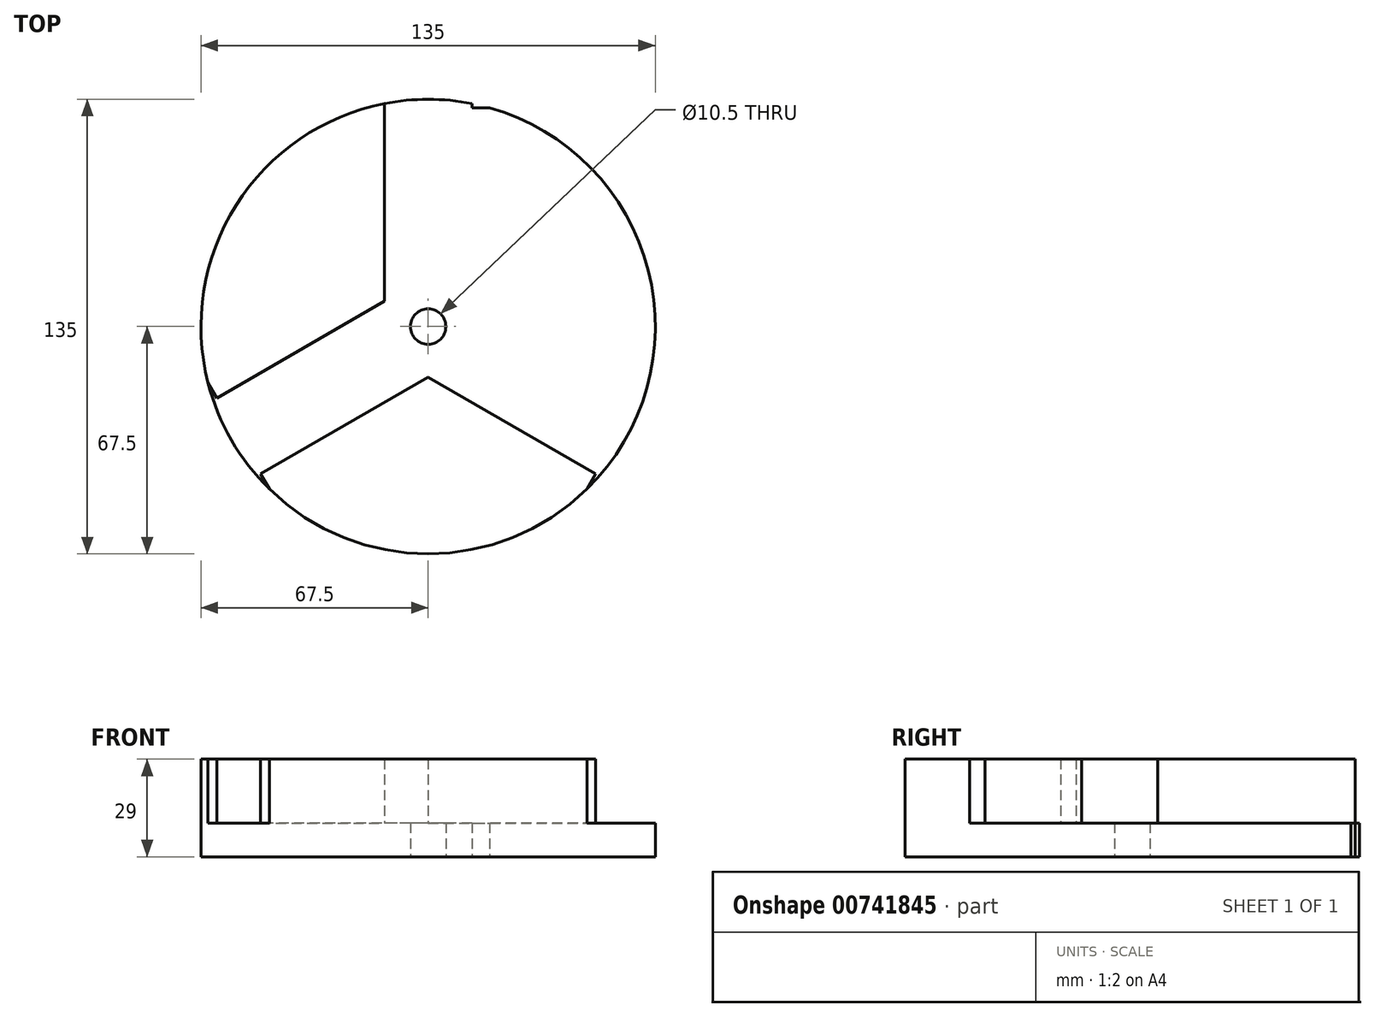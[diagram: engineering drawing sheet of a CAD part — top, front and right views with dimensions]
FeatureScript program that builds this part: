
annotation { "Feature Type Name" : "Feature", "Feature Type Description" : "" }
export const myFeature = defineFeature(function(context is Context, id is Id, definition is map)
    precondition{}
    {
        {
            var Q0;
            Q0=qCreatedBy(makeId("Top.planeOp"),FACE);
            var sketch = newSketch(context, id + "F0", { "sketchPlane" : qUnion([Q0])});
            skCircle(sketch, "E0", {"center": v(0, 0) * mm, "radius": 67.5 * mm});
            skCircle(sketch, "E1", {"center": v(0, 0) * mm, "radius": 5.25 * mm});
            skCircle(sketch, "E2", {"center": v(0, 0) * mm, "radius": 13 * mm});
            skLineSegment(sketch, "E3.top", {"start": v(-13, 70) * mm, "end": v(13, 70) * mm});
            skLineSegment(sketch, "E3.left", {"start": v(-13, 0) * mm, "end": v(-13, 70) * mm});
            skLineSegment(sketch, "E3.right", {"start": v(13, 0) * mm, "end": v(13, 70) * mm});
            skLineSegment(sketch, "E4", {"start": v(-6.5, 11.26) * mm, "end": v(-67.12, -23.74) * mm});
            skLineSegment(sketch, "E5", {"start": v(-67.12, -23.74) * mm, "end": v(-54.12, -46.26) * mm});
            skLineSegment(sketch, "E6", {"start": v(-54.12, -46.26) * mm, "end": v(6.5, -11.26) * mm});
            skLineSegment(sketch, "E7", {"start": v(6.5, 11.26) * mm, "end": v(67.12, -23.74) * mm});
            skLineSegment(sketch, "E8", {"start": v(67.12, -23.74) * mm, "end": v(54.12, -46.26) * mm});
            skLineSegment(sketch, "E9", {"start": v(54.12, -46.26) * mm, "end": v(-6.5, -11.26) * mm});
            skLineSegment(sketch, "E10", {"start": v(66.88, -14.17) * mm, "end": v(46.54, -49.38) * mm});
            skLineSegment(sketch, "E11", {"start": v(-65.4, -16.74) * mm, "end": v(-45.17, -51.75) * mm});
            skLineSegment(sketch, "E12", {"start": v(-20.7, 65) * mm, "end": v(22.29, 65) * mm});
            skCircle(sketch, "E13", {"center": v(0, 0) * mm, "radius": 6.25 * mm});
            skLineSegment(sketch, "E14", {"start": v(-13, 7.5) * mm, "end": v(-62.8, -21.24) * mm});
            skSolve(sketch);
        }
        {
            var Q0;
            {var subQ0=sQuery(id+"F0.wireOp",EDGE,"E12");var subQ1=sQuery(id+"F0.wireOp",EDGE,"E0");var subQ2=makeQuery(id+"F0.imprint","INTERSECT",VERTEX,{"disambiguationData":[OD(0.0)],"derivedFrom":[subQ1,subQ0]});Q0=makeQuery(id+"F0.imprint","IMPRINT",FACE,{"disambiguationData":[TD([[makeQuery(id+"F0.imprint","IMPRINT",EDGE,{"disambiguationData":[TD([[subQ2,-1.0]])],"derivedFrom":subQ1}),1.0]])]});}
            var Q1;
            {var subQ0=sQuery(id+"F0.wireOp",EDGE,"E12");var subQ1=sQuery(id+"F0.wireOp",EDGE,"E0");var subQ2=makeQuery(id+"F0.imprint","INTERSECT",VERTEX,{"disambiguationData":[OD(1.0)],"derivedFrom":[subQ1,subQ0]});Q1=makeQuery(id+"F0.imprint","IMPRINT",FACE,{"disambiguationData":[TD([[makeQuery(id+"F0.imprint","IMPRINT",EDGE,{"disambiguationData":[TD([[subQ2,1.0]])],"derivedFrom":subQ1}),1.0]])]});}
            var Q2;
            {var subQ0=sQuery(id+"F0.wireOp",EDGE,"E11");var subQ1=sQuery(id+"F0.wireOp",EDGE,"E0");var subQ2=makeQuery(id+"F0.imprint","INTERSECT",VERTEX,{"disambiguationData":[OD(0.0)],"derivedFrom":[subQ1,subQ0]});Q2=makeQuery(id+"F0.imprint","IMPRINT",FACE,{"disambiguationData":[TD([[makeQuery(id+"F0.imprint","IMPRINT",EDGE,{"disambiguationData":[TD([[subQ2,-1.0]])],"derivedFrom":subQ1}),1.0]])]});}
            var Q3;
            {var subQ0=sQuery(id+"F0.wireOp",EDGE,"E11");var subQ1=sQuery(id+"F0.wireOp",EDGE,"E0");var subQ2=makeQuery(id+"F0.imprint","INTERSECT",VERTEX,{"disambiguationData":[OD(1.0)],"derivedFrom":[subQ1,subQ0]});Q3=makeQuery(id+"F0.imprint","IMPRINT",FACE,{"disambiguationData":[TD([[makeQuery(id+"F0.imprint","IMPRINT",EDGE,{"disambiguationData":[TD([[subQ2,1.0]])],"derivedFrom":subQ1}),1.0]])]});}
            var Q4;
            {var subQ0=sQuery(id+"F0.wireOp",EDGE,"E10");var subQ1=sQuery(id+"F0.wireOp",EDGE,"E0");var subQ2=makeQuery(id+"F0.imprint","INTERSECT",VERTEX,{"disambiguationData":[OD(0.0)],"derivedFrom":[subQ1,subQ0]});Q4=makeQuery(id+"F0.imprint","IMPRINT",FACE,{"disambiguationData":[TD([[makeQuery(id+"F0.imprint","IMPRINT",EDGE,{"disambiguationData":[TD([[subQ2,-1.0]])],"derivedFrom":subQ1}),1.0]])]});}
            var Q5;
            {var subQ0=sQuery(id+"F0.wireOp",EDGE,"E10");var subQ1=sQuery(id+"F0.wireOp",EDGE,"E0");var subQ2=makeQuery(id+"F0.imprint","INTERSECT",VERTEX,{"disambiguationData":[OD(1.0)],"derivedFrom":[subQ1,subQ0]});Q5=makeQuery(id+"F0.imprint","IMPRINT",FACE,{"disambiguationData":[TD([[makeQuery(id+"F0.imprint","IMPRINT",EDGE,{"disambiguationData":[TD([[subQ2,1.0]])],"derivedFrom":subQ1}),1.0]])]});}
            var Q6;
            {var subQ5=sQuery(id+"F0.wireOp",EDGE,"E11");var subQ6=sQuery(id+"F0.wireOp",EDGE,"E0");var subQ7=makeQuery(id+"F0.imprint","INTERSECT",VERTEX,{"disambiguationData":[OD(0.0)],"derivedFrom":[subQ6,subQ5]});Q6=makeQuery(id+"F0.imprint","IMPRINT",FACE,{"disambiguationData":[TD([[makeQuery(id+"F0.imprint","IMPRINT",EDGE,{"disambiguationData":[TD([[subQ7,1.0]])],"derivedFrom":subQ6}),1.0]])]});}
            var Q7;
            {var subQ0=sQuery(id+"F0.wireOp",EDGE,"E4");var subQ1=sQuery(id+"F0.wireOp",EDGE,"E0");var subQ2=makeQuery(id+"F0.imprint","INTERSECT",VERTEX,{"derivedFrom":[subQ1,subQ0]});Q7=makeQuery(id+"F0.imprint","IMPRINT",FACE,{"disambiguationData":[TD([[makeQuery(id+"F0.imprint","IMPRINT",EDGE,{"disambiguationData":[TD([[subQ2,-1.0]])],"derivedFrom":subQ1}),1.0]])]});}
            var Q8;
            {var subQ5=sQuery(id+"F0.wireOp",EDGE,"E11");var subQ7=sQuery(id+"F0.wireOp",EDGE,"E0");var subQ9=makeQuery(id+"F0.imprint","INTERSECT",VERTEX,{"disambiguationData":[OD(1.0)],"derivedFrom":[subQ7,subQ5]});Q8=makeQuery(id+"F0.imprint","IMPRINT",FACE,{"disambiguationData":[TD([[makeQuery(id+"F0.imprint","IMPRINT",EDGE,{"disambiguationData":[TD([[subQ9,-1.0]])],"derivedFrom":subQ7}),1.0]])]});}
            var Q9;
            {var subQ0=sQuery(id+"F0.wireOp",EDGE,"E9");var subQ1=sQuery(id+"F0.wireOp",EDGE,"E0");var subQ2=makeQuery(id+"F0.imprint","INTERSECT",VERTEX,{"derivedFrom":[subQ1,subQ0]});Q9=makeQuery(id+"F0.imprint","IMPRINT",FACE,{"disambiguationData":[TD([[makeQuery(id+"F0.imprint","IMPRINT",EDGE,{"disambiguationData":[TD([[subQ2,-1.0]])],"derivedFrom":subQ1}),1.0]])]});}
            var Q10;
            {var subQ1=sQuery(id+"F0.wireOp",EDGE,"E0");var subQ7=sQuery(id+"F0.wireOp",EDGE,"E12");var subQ9=makeQuery(id+"F0.imprint","INTERSECT",VERTEX,{"disambiguationData":[OD(0.0)],"derivedFrom":[subQ1,subQ7]});Q10=makeQuery(id+"F0.imprint","IMPRINT",FACE,{"disambiguationData":[TD([[makeQuery(id+"F0.imprint","IMPRINT",EDGE,{"disambiguationData":[TD([[subQ9,1.0]])],"derivedFrom":subQ1}),1.0]])]});}
            var Q11;
            {var subQ0=sQuery(id+"F0.wireOp",EDGE,"E4");var subQ1=sQuery(id+"F0.wireOp",EDGE,"E2");var subQ2=makeQuery(id+"F0.imprint","INTERSECT",VERTEX,{"derivedFrom":[subQ1,subQ0]});Q11=makeQuery(id+"F0.imprint","IMPRINT",FACE,{"disambiguationData":[TD([[makeQuery(id+"F0.imprint","IMPRINT",EDGE,{"disambiguationData":[TD([[subQ2,1.0]])],"derivedFrom":subQ1}),-1.0]])]});}
            var Q12;
            {var subQ0=sQuery(id+"F0.wireOp",EDGE,"E3.right");var subQ1=sQuery(id+"F0.wireOp",EDGE,"E0");var subQ2=makeQuery(id+"F0.imprint","INTERSECT",VERTEX,{"derivedFrom":[subQ1,subQ0]});Q12=makeQuery(id+"F0.imprint","IMPRINT",FACE,{"disambiguationData":[TD([[makeQuery(id+"F0.imprint","IMPRINT",EDGE,{"disambiguationData":[TD([[subQ2,-1.0]])],"derivedFrom":subQ1}),1.0]])]});}
            var Q13;
            {var subQ0=sQuery(id+"F0.wireOp",EDGE,"E3.bottom");var subQ6=sQuery(id+"F0.wireOp",EDGE,"E1");var subQ7=makeQuery(id+"F0.imprint","INTERSECT",VERTEX,{"disambiguationData":[OD(0.0)],"derivedFrom":[subQ6,subQ0]});Q13=makeQuery(id+"F0.imprint","IMPRINT",FACE,{"disambiguationData":[TD([[makeQuery(id+"F0.imprint","IMPRINT",EDGE,{"disambiguationData":[TD([[subQ7,-1.0]])],"derivedFrom":subQ6}),-1.0]])]});}
            var Q14;
            {var subQ0=sQuery(id+"F0.wireOp",EDGE,"E4");var subQ1=sQuery(id+"F0.wireOp",EDGE,"E3.left");var subQ2=makeQuery(id+"F0.imprint","INTERSECT",VERTEX,{"derivedFrom":[subQ1,subQ0]});Q14=makeQuery(id+"F0.imprint","IMPRINT",FACE,{"disambiguationData":[TD([[makeQuery(id+"F0.imprint","IMPRINT",EDGE,{"disambiguationData":[TD([[subQ2,-1.0]])],"derivedFrom":subQ0}),1.0]])]});}
            var Q15;
            {var subQ0=sQuery(id+"F0.wireOp",EDGE,"E6");var subQ1=sQuery(id+"F0.wireOp",EDGE,"E2");var subQ2=makeQuery(id+"F0.imprint","INTERSECT",VERTEX,{"derivedFrom":[subQ1,subQ0]});Q15=makeQuery(id+"F0.imprint","IMPRINT",FACE,{"disambiguationData":[TD([[makeQuery(id+"F0.imprint","IMPRINT",EDGE,{"disambiguationData":[TD([[subQ2,1.0]])],"derivedFrom":subQ1}),-1.0]])]});}
            var Q16;
            {var subQ1=sQuery(id+"F0.wireOp",EDGE,"E2");var subQ3=sQuery(id+"F0.wireOp",EDGE,"E4");var subQ4=makeQuery(id+"F0.imprint","INTERSECT",VERTEX,{"derivedFrom":[subQ1,subQ3]});Q16=makeQuery(id+"F0.imprint","IMPRINT",FACE,{"disambiguationData":[TD([[makeQuery(id+"F0.imprint","IMPRINT",EDGE,{"disambiguationData":[TD([[subQ4,-1.0]])],"derivedFrom":subQ3}),1.0]])]});}
            var Q17;
            {var subQ1=sQuery(id+"F0.wireOp",EDGE,"E2");var subQ3=sQuery(id+"F0.wireOp",EDGE,"E7");var subQ4=makeQuery(id+"F0.imprint","INTERSECT",VERTEX,{"derivedFrom":[subQ1,subQ3]});Q17=makeQuery(id+"F0.imprint","IMPRINT",FACE,{"disambiguationData":[TD([[makeQuery(id+"F0.imprint","IMPRINT",EDGE,{"disambiguationData":[TD([[subQ4,-1.0]])],"derivedFrom":subQ3}),-1.0]])]});}
            var Q18;
            {var subQ0=sQuery(id+"F0.wireOp",EDGE,"E3.bottom");var subQ6=sQuery(id+"F0.wireOp",EDGE,"E1");var subQ7=makeQuery(id+"F0.imprint","INTERSECT",VERTEX,{"disambiguationData":[OD(0.0)],"derivedFrom":[subQ6,subQ0]});Q18=makeQuery(id+"F0.imprint","IMPRINT",FACE,{"disambiguationData":[TD([[makeQuery(id+"F0.imprint","IMPRINT",EDGE,{"disambiguationData":[TD([[subQ7,1.0]])],"derivedFrom":subQ6}),-1.0]])]});}
            var Q19;
            {var subQ5=sQuery(id+"F0.wireOp",EDGE,"E6");var subQ6=sQuery(id+"F0.wireOp",EDGE,"E2");var subQ7=makeQuery(id+"F0.imprint","INTERSECT",VERTEX,{"derivedFrom":[subQ6,subQ5]});Q19=makeQuery(id+"F0.imprint","IMPRINT",FACE,{"disambiguationData":[TD([[makeQuery(id+"F0.imprint","IMPRINT",EDGE,{"disambiguationData":[TD([[subQ7,1.0]])],"derivedFrom":subQ5}),-1.0]])]});}
            var Q20;
            {var subQ0=sQuery(id+"F0.wireOp",EDGE,"E2");var subQ1=makeQuery(id+"F0.imprint","INTERSECT",VERTEX,{"derivedFrom":[subQ0,sQuery(id+"F0.wireOp",EDGE,"E7")]});Q20=makeQuery(id+"F0.imprint","IMPRINT",FACE,{"disambiguationData":[TD([[makeQuery(id+"F0.imprint","IMPRINT",EDGE,{"disambiguationData":[TD([[subQ1,1.0]])],"derivedFrom":subQ0}),1.0]])]});}
            var Q21;
            {var subQ0=sQuery(id+"F0.wireOp",EDGE,"E2");var subQ1=makeQuery(id+"F0.imprint","INTERSECT",VERTEX,{"derivedFrom":[subQ0,sQuery(id+"F0.wireOp",EDGE,"E6")]});Q21=makeQuery(id+"F0.imprint","IMPRINT",FACE,{"disambiguationData":[TD([[makeQuery(id+"F0.imprint","IMPRINT",EDGE,{"disambiguationData":[TD([[subQ1,1.0]])],"derivedFrom":subQ0}),1.0]])]});}
            var Q22;
            {var subQ1=sQuery(id+"F0.wireOp",EDGE,"E2");var subQ3=sQuery(id+"F0.wireOp",EDGE,"MO3U9A4Q-gPJx-rqol-o6lv-NwqyU01XIywo");var subQ4=makeQuery(id+"F0.imprint","INTERSECT",VERTEX,{"disambiguationData":[OD(0.0)],"derivedFrom":[subQ1,subQ3]});Q22=makeQuery(id+"F0.imprint","IMPRINT",FACE,{"disambiguationData":[TD([[makeQuery(id+"F0.imprint","IMPRINT",EDGE,{"disambiguationData":[TD([[subQ4,-1.0]])],"derivedFrom":subQ3}),1.0]])]});}
            var Q23;
            {var subQ1=sQuery(id+"F0.wireOp",EDGE,"E2");var subQ3=sQuery(id+"F0.wireOp",EDGE,"MO3U9A4Q-gPJx-rqol-o6lv-NwqyU01XIywo");var subQ4=makeQuery(id+"F0.imprint","INTERSECT",VERTEX,{"disambiguationData":[OD(0.0)],"derivedFrom":[subQ1,subQ3]});Q23=makeQuery(id+"F0.imprint","IMPRINT",FACE,{"disambiguationData":[TD([[makeQuery(id+"F0.imprint","IMPRINT",EDGE,{"disambiguationData":[TD([[subQ4,1.0]])],"derivedFrom":subQ1}),-1.0]])]});}
            var Q24;
            {var subQ0=sQuery(id+"F0.wireOp",EDGE,"MO3U9A4Q-gPJx-rqol-o6lv-NwqyU01XIywo");var subQ1=sQuery(id+"F0.wireOp",EDGE,"E2");var subQ2=makeQuery(id+"F0.imprint","INTERSECT",VERTEX,{"disambiguationData":[OD(0.0)],"derivedFrom":[subQ1,subQ0]});Q24=makeQuery(id+"F0.imprint","IMPRINT",FACE,{"disambiguationData":[TD([[makeQuery(id+"F0.imprint","IMPRINT",EDGE,{"disambiguationData":[TD([[subQ2,-1.0]])],"derivedFrom":subQ1}),-1.0]])]});}
            var Q25;
            {var subQ0=sQuery(id+"F0.wireOp",EDGE,"QYsPJi62-LnfM-lreK-0qqD-Sy3b8xS6lFHo");var subQ1=sQuery(id+"F0.wireOp",EDGE,"E2");var subQ2=makeQuery(id+"F0.imprint","INTERSECT",VERTEX,{"disambiguationData":[OD(1.0)],"derivedFrom":[subQ1,subQ0]});Q25=makeQuery(id+"F0.imprint","IMPRINT",FACE,{"disambiguationData":[TD([[makeQuery(id+"F0.imprint","IMPRINT",EDGE,{"disambiguationData":[TD([[subQ2,-1.0]])],"derivedFrom":subQ1}),-1.0]])]});}
            var Q26;
            {var subQ1=sQuery(id+"F0.wireOp",EDGE,"E2");var subQ3=sQuery(id+"F0.wireOp",EDGE,"QYsPJi62-LnfM-lreK-0qqD-Sy3b8xS6lFHo");var subQ4=makeQuery(id+"F0.imprint","INTERSECT",VERTEX,{"disambiguationData":[OD(0.0)],"derivedFrom":[subQ1,subQ3]});Q26=makeQuery(id+"F0.imprint","IMPRINT",FACE,{"disambiguationData":[TD([[makeQuery(id+"F0.imprint","IMPRINT",EDGE,{"disambiguationData":[TD([[subQ4,1.0]])],"derivedFrom":subQ3}),1.0]])]});}
            var Q27;
            {var subQ1=sQuery(id+"F0.wireOp",EDGE,"E2");var subQ3=sQuery(id+"F0.wireOp",EDGE,"QYsPJi62-LnfM-lreK-0qqD-Sy3b8xS6lFHo");var subQ4=makeQuery(id+"F0.imprint","INTERSECT",VERTEX,{"disambiguationData":[OD(0.0)],"derivedFrom":[subQ1,subQ3]});Q27=makeQuery(id+"F0.imprint","IMPRINT",FACE,{"disambiguationData":[TD([[makeQuery(id+"F0.imprint","IMPRINT",EDGE,{"disambiguationData":[TD([[subQ4,-1.0]])],"derivedFrom":subQ1}),-1.0]])]});}
            var Q28;
            {var subQ0=sQuery(id+"F0.wireOp",EDGE,"G14e21PV-Cuiq-R80L-tFCo-INJSukK78Nln");var subQ1=sQuery(id+"F0.wireOp",EDGE,"E2");var subQ2=makeQuery(id+"F0.imprint","INTERSECT",VERTEX,{"disambiguationData":[OD(1.0)],"derivedFrom":[subQ1,subQ0]});Q28=makeQuery(id+"F0.imprint","IMPRINT",FACE,{"disambiguationData":[TD([[makeQuery(id+"F0.imprint","IMPRINT",EDGE,{"disambiguationData":[TD([[subQ2,-1.0]])],"derivedFrom":subQ1}),-1.0]])]});}
            var Q29;
            {var subQ1=sQuery(id+"F0.wireOp",EDGE,"E2");var subQ3=makeQuery(id+"F0.imprint","INTERSECT",VERTEX,{"derivedFrom":[subQ1,sQuery(id+"F0.wireOp",EDGE,"E9")]});Q29=makeQuery(id+"F0.imprint","IMPRINT",FACE,{"disambiguationData":[TD([[makeQuery(id+"F0.imprint","IMPRINT",EDGE,{"disambiguationData":[TD([[subQ3,-1.0]])],"derivedFrom":subQ1}),1.0]])]});}
            var Q30;
            {var subQ0=sQuery(id+"F0.wireOp",EDGE,"E9");var subQ1=sQuery(id+"F0.wireOp",EDGE,"E2");var subQ2=makeQuery(id+"F0.imprint","INTERSECT",VERTEX,{"derivedFrom":[subQ1,subQ0]});Q30=makeQuery(id+"F0.imprint","IMPRINT",FACE,{"disambiguationData":[TD([[makeQuery(id+"F0.imprint","IMPRINT",EDGE,{"disambiguationData":[TD([[subQ2,-1.0]])],"derivedFrom":subQ1}),-1.0]])]});}
            var Q31;
            {var subQ5=sQuery(id+"F0.wireOp",EDGE,"HD1IVMyh-0AOR-znRN-wXrD-2HfL0jaRWnpP");var subQ6=sQuery(id+"F0.wireOp",EDGE,"E4");var subQ7=makeQuery(id+"F0.imprint","INTERSECT",VERTEX,{"derivedFrom":[subQ6,subQ5]});Q31=makeQuery(id+"F0.imprint","IMPRINT",FACE,{"disambiguationData":[TD([[makeQuery(id+"F0.imprint","IMPRINT",EDGE,{"disambiguationData":[TD([[subQ7,-1.0]])],"derivedFrom":subQ6}),1.0]])]});}
            var Q32;
            {var subQ1=sQuery(id+"F0.wireOp",EDGE,"E3.left");var subQ3=sQuery(id+"F0.wireOp",EDGE,"BKccuNU5-A43L-LsUo-uLtq-IYICvbiabubH");var subQ4=makeQuery(id+"F0.imprint","INTERSECT",VERTEX,{"derivedFrom":[subQ1,subQ3]});Q32=makeQuery(id+"F0.imprint","IMPRINT",FACE,{"disambiguationData":[TD([[makeQuery(id+"F0.imprint","IMPRINT",EDGE,{"disambiguationData":[TD([[subQ4,1.0]])],"derivedFrom":subQ3}),1.0]])]});}
            var Q33;
            {var subQ0=sQuery(id+"F0.wireOp",EDGE,"G14e21PV-Cuiq-R80L-tFCo-INJSukK78Nln");var subQ3=sQuery(id+"F0.wireOp",EDGE,"BKccuNU5-A43L-LsUo-uLtq-IYICvbiabubH");var subQ5=makeQuery(id+"F0.imprint","INTERSECT",VERTEX,{"derivedFrom":[subQ0,subQ3]});Q33=makeQuery(id+"F0.imprint","IMPRINT",FACE,{"disambiguationData":[TD([[makeQuery(id+"F0.imprint","IMPRINT",EDGE,{"disambiguationData":[TD([[subQ5,-1.0]])],"derivedFrom":subQ3}),1.0]])]});}
            var Q34;
            {var subQ0=sQuery(id+"F0.wireOp",EDGE,"QYsPJi62-LnfM-lreK-0qqD-Sy3b8xS6lFHo");var subQ3=sQuery(id+"F0.wireOp",EDGE,"HD1IVMyh-0AOR-znRN-wXrD-2HfL0jaRWnpP");var subQ5=makeQuery(id+"F0.imprint","INTERSECT",VERTEX,{"derivedFrom":[subQ0,subQ3]});Q34=makeQuery(id+"F0.imprint","IMPRINT",FACE,{"disambiguationData":[TD([[makeQuery(id+"F0.imprint","IMPRINT",EDGE,{"disambiguationData":[TD([[subQ5,-1.0]])],"derivedFrom":subQ3}),-1.0]])]});}
            var Q35;
            {var subQ0=sQuery(id+"F0.wireOp",EDGE,"QYsPJi62-LnfM-lreK-0qqD-Sy3b8xS6lFHo");var subQ3=sQuery(id+"F0.wireOp",EDGE,"fLDxUA22-G8zE-o3Cl-MvxH-7l2fgcETCKwE");var subQ5=makeQuery(id+"F0.imprint","INTERSECT",VERTEX,{"derivedFrom":[subQ0,subQ3]});Q35=makeQuery(id+"F0.imprint","IMPRINT",FACE,{"disambiguationData":[TD([[makeQuery(id+"F0.imprint","IMPRINT",EDGE,{"disambiguationData":[TD([[subQ5,1.0]])],"derivedFrom":subQ3}),-1.0]])]});}
            var Q36;
            {var subQ1=sQuery(id+"F0.wireOp",EDGE,"E6");var subQ3=sQuery(id+"F0.wireOp",EDGE,"fLDxUA22-G8zE-o3Cl-MvxH-7l2fgcETCKwE");var subQ4=makeQuery(id+"F0.imprint","INTERSECT",VERTEX,{"derivedFrom":[subQ1,subQ3]});Q36=makeQuery(id+"F0.imprint","IMPRINT",FACE,{"disambiguationData":[TD([[makeQuery(id+"F0.imprint","IMPRINT",EDGE,{"disambiguationData":[TD([[subQ4,-1.0]])],"derivedFrom":subQ3}),-1.0]])]});}
            var Q37;
            {var subQ0=sQuery(id+"F0.wireOp",EDGE,"E9");var subQ3=sQuery(id+"F0.wireOp",EDGE,"ui7POcHa-QiDH-AwLJ-at4n-CY1uFXcPNaNc");var subQ5=makeQuery(id+"F0.imprint","INTERSECT",VERTEX,{"derivedFrom":[subQ0,subQ3]});Q37=makeQuery(id+"F0.imprint","IMPRINT",FACE,{"disambiguationData":[TD([[makeQuery(id+"F0.imprint","IMPRINT",EDGE,{"disambiguationData":[TD([[subQ5,-1.0]])],"derivedFrom":subQ3}),1.0]])]});}
            var Q38;
            {var subQ0=sQuery(id+"F0.wireOp",EDGE,"MO3U9A4Q-gPJx-rqol-o6lv-NwqyU01XIywo");var subQ3=sQuery(id+"F0.wireOp",EDGE,"ui7POcHa-QiDH-AwLJ-at4n-CY1uFXcPNaNc");var subQ5=makeQuery(id+"F0.imprint","INTERSECT",VERTEX,{"derivedFrom":[subQ0,subQ3]});Q38=makeQuery(id+"F0.imprint","IMPRINT",FACE,{"disambiguationData":[TD([[makeQuery(id+"F0.imprint","IMPRINT",EDGE,{"disambiguationData":[TD([[subQ5,1.0]])],"derivedFrom":subQ3}),1.0]])]});}
            var Q39;
            {var subQ0=sQuery(id+"F0.wireOp",EDGE,"E7");var subQ3=sQuery(id+"F0.wireOp",EDGE,"rcE8XYTH-bGtv-JclR-0KPA-zKxhDnFdQM1I");var subQ5=makeQuery(id+"F0.imprint","INTERSECT",VERTEX,{"derivedFrom":[subQ0,subQ3]});Q39=makeQuery(id+"F0.imprint","IMPRINT",FACE,{"disambiguationData":[TD([[makeQuery(id+"F0.imprint","IMPRINT",EDGE,{"disambiguationData":[TD([[subQ5,-1.0]])],"derivedFrom":subQ3}),-1.0]])]});}
            var Q40;
            {var subQ0=sQuery(id+"F0.wireOp",EDGE,"MO3U9A4Q-gPJx-rqol-o6lv-NwqyU01XIywo");var subQ3=sQuery(id+"F0.wireOp",EDGE,"rcE8XYTH-bGtv-JclR-0KPA-zKxhDnFdQM1I");var subQ5=makeQuery(id+"F0.imprint","INTERSECT",VERTEX,{"derivedFrom":[subQ0,subQ3]});Q40=makeQuery(id+"F0.imprint","IMPRINT",FACE,{"disambiguationData":[TD([[makeQuery(id+"F0.imprint","IMPRINT",EDGE,{"disambiguationData":[TD([[subQ5,1.0]])],"derivedFrom":subQ3}),-1.0]])]});}
            var Q41;
            {var subQ0=sQuery(id+"F0.wireOp",EDGE,"G14e21PV-Cuiq-R80L-tFCo-INJSukK78Nln");var subQ3=sQuery(id+"F0.wireOp",EDGE,"HvymFqe2-4WWB-SfJQ-fLVT-cQMT8DMhy66K");var subQ5=makeQuery(id+"F0.imprint","INTERSECT",VERTEX,{"derivedFrom":[subQ0,subQ3]});Q41=makeQuery(id+"F0.imprint","IMPRINT",FACE,{"disambiguationData":[TD([[makeQuery(id+"F0.imprint","IMPRINT",EDGE,{"disambiguationData":[TD([[subQ5,-1.0]])],"derivedFrom":subQ3}),-1.0]])]});}
            var Q42;
            {var subQ1=sQuery(id+"F0.wireOp",EDGE,"E3.right");var subQ3=sQuery(id+"F0.wireOp",EDGE,"HvymFqe2-4WWB-SfJQ-fLVT-cQMT8DMhy66K");var subQ4=makeQuery(id+"F0.imprint","INTERSECT",VERTEX,{"derivedFrom":[subQ1,subQ3]});Q42=makeQuery(id+"F0.imprint","IMPRINT",FACE,{"disambiguationData":[TD([[makeQuery(id+"F0.imprint","IMPRINT",EDGE,{"disambiguationData":[TD([[subQ4,1.0]])],"derivedFrom":subQ3}),-1.0]])]});}
            var Q43;
            {var subQ5=sQuery(id+"F0.wireOp",EDGE,"E14");Q43=makeQuery(id+"F0.imprint","IMPRINT",FACE,{"disambiguationData":[TD([[makeQuery(id+"F0.imprint","IMPRINT",EDGE,{"derivedFrom":subQ5}),1.0]])]});}
            extrude(context, id + "F1", {"entities" : qUnion([Q0, Q1, Q2, Q3, Q4, Q5, Q6, Q7, Q8, Q9, Q10, Q11, Q12, Q13, Q14, Q15, Q16, Q17, Q18, Q19, Q20, Q21, Q22, Q23, Q24, Q25, Q26, Q27, Q28, Q29, Q30, Q31, Q32, Q33, Q34, Q35, Q36, Q37, Q38, Q39, Q40, Q41, Q42, Q43]), "depth" : 10 * mm, "offsetDistance" : 25 * mm});
        }
        {
            var Q0;
            {var subQ5=sQuery(id+"F0.wireOp",EDGE,"E11");var subQ6=sQuery(id+"F0.wireOp",EDGE,"E0");var subQ7=makeQuery(id+"F0.imprint","INTERSECT",VERTEX,{"disambiguationData":[OD(0.0)],"derivedFrom":[subQ6,subQ5]});Q0=makeQuery(id+"F0.imprint","IMPRINT",FACE,{"disambiguationData":[TD([[makeQuery(id+"F0.imprint","IMPRINT",EDGE,{"disambiguationData":[TD([[subQ7,1.0]])],"derivedFrom":subQ6}),1.0]])]});}
            var Q1;
            {var subQ5=sQuery(id+"F0.wireOp",EDGE,"E11");var subQ7=sQuery(id+"F0.wireOp",EDGE,"E0");var subQ9=makeQuery(id+"F0.imprint","INTERSECT",VERTEX,{"disambiguationData":[OD(1.0)],"derivedFrom":[subQ7,subQ5]});Q1=makeQuery(id+"F0.imprint","IMPRINT",FACE,{"disambiguationData":[TD([[makeQuery(id+"F0.imprint","IMPRINT",EDGE,{"disambiguationData":[TD([[subQ9,-1.0]])],"derivedFrom":subQ7}),1.0]])]});}
            var Q2;
            {var subQ1=sQuery(id+"F0.wireOp",EDGE,"E0");var subQ7=sQuery(id+"F0.wireOp",EDGE,"E12");var subQ9=makeQuery(id+"F0.imprint","INTERSECT",VERTEX,{"disambiguationData":[OD(0.0)],"derivedFrom":[subQ1,subQ7]});Q2=makeQuery(id+"F0.imprint","IMPRINT",FACE,{"disambiguationData":[TD([[makeQuery(id+"F0.imprint","IMPRINT",EDGE,{"disambiguationData":[TD([[subQ9,1.0]])],"derivedFrom":subQ1}),1.0]])]});}
            extrude(context, id + "F2", {"entities" : qUnion([Q0, Q1, Q2]), "operationType" : NewBodyOperationType.ADD, "depth" : 29 * mm, "offsetDistance" : 25 * mm});
        }
    });
